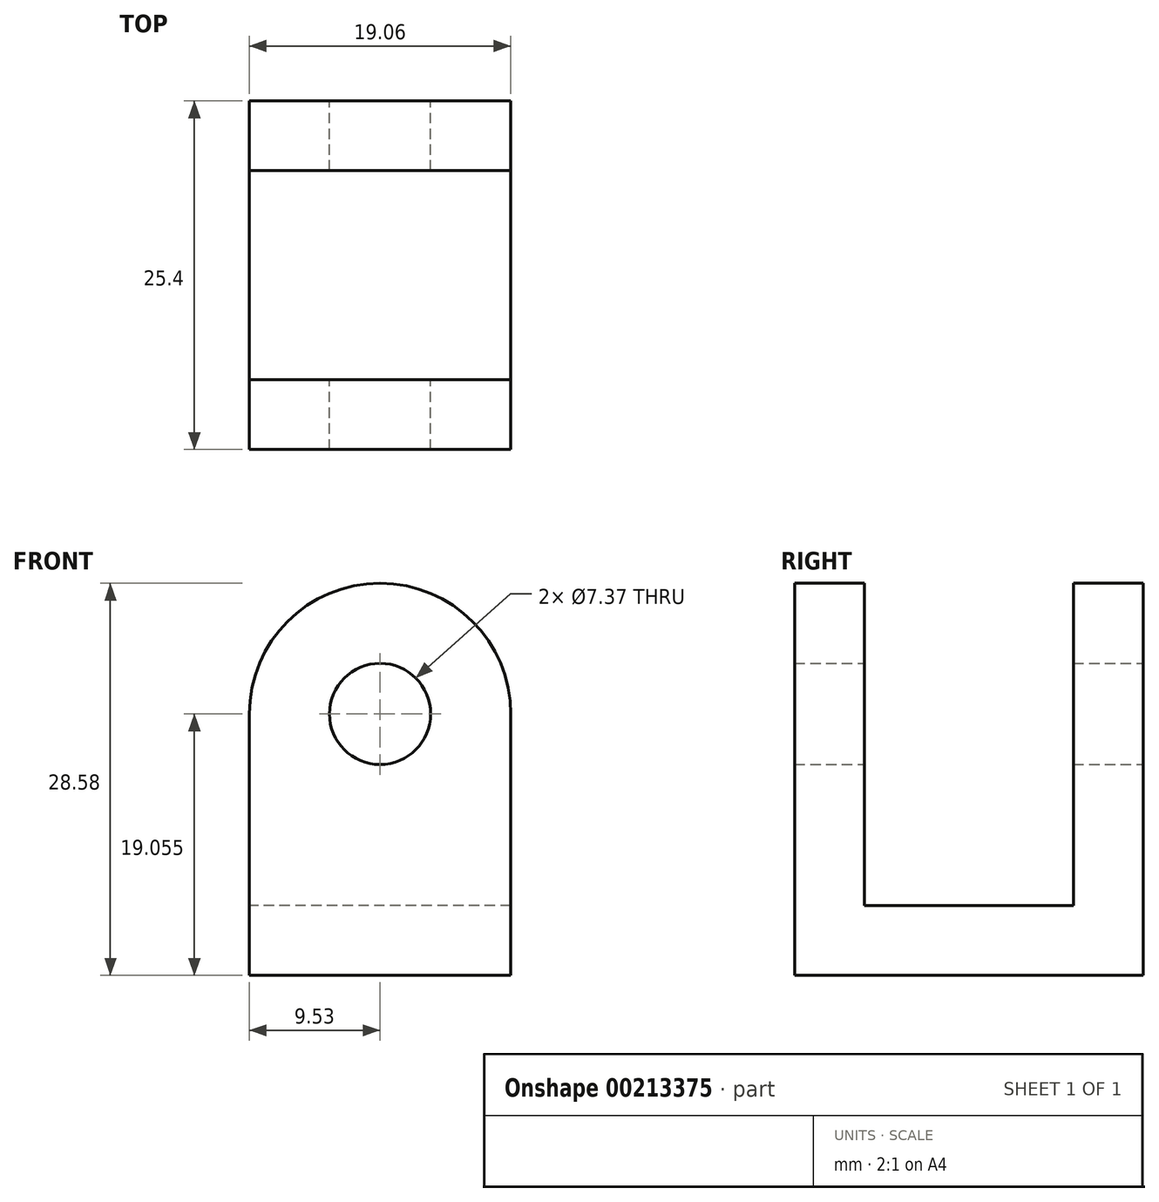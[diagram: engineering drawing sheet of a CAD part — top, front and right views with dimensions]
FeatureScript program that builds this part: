
annotation { "Feature Type Name" : "Feature", "Feature Type Description" : "" }
export const myFeature = defineFeature(function(context is Context, id is Id, definition is map)
    precondition{}
    {
        {
            var Q0;
            Q0=qCreatedBy(makeId("Front.planeOp"),FACE);
            var sketch = newSketch(context, id + "F0", { "sketchPlane" : qUnion([Q0])});
            skLineSegment(sketch, "E0.bottom", {"start": v(9.53, 9.53) * mm, "end": v(-9.52, 9.53) * mm});
            skLineSegment(sketch, "E0.top", {"start": v(9.52, -9.53) * mm, "end": v(-9.53, -9.53) * mm});
            skLineSegment(sketch, "E0.left", {"start": v(9.53, 9.53) * mm, "end": v(9.52, -9.53) * mm});
            skLineSegment(sketch, "E0.right", {"start": v(-9.52, 9.53) * mm, "end": v(-9.53, -9.53) * mm});
            skPoint(sketch, "E0.middle", {"position": v(0, 0) * mm});
            skCircle(sketch, "E1", {"center": v(0, 9.53) * mm, "radius": 9.53 * mm});
            skCircle(sketch, "E2", {"center": v(0, 9.53) * mm, "radius": 3.69 * mm});
            skSolve(sketch);
        }
        {
            var Q0;
            {var subQ0=sQuery(id+"F0.wireOp",EDGE,"E0.bottom");Q0=makeQuery(id+"F0.imprint","IMPRINT",FACE,{"disambiguationData":[TD([[makeQuery(id+"F0.imprint","IMPRINT",EDGE,{"derivedFrom":subQ0}),-1.0]])]});}
            var Q1;
            Q1=makeQuery(id+"F0.imprint","IMPRINT",FACE,{"disambiguationData":[TD([[makeQuery(id+"F0.imprint","IMPRINT",EDGE,{"derivedFrom":sQuery(id+"F0.wireOp",EDGE,"E0.top")}),-1.0]])]});
            var Q2;
            {var subQ0=sQuery(id+"F0.wireOp",EDGE,"E0.bottom");Q2=makeQuery(id+"F0.imprint","IMPRINT",FACE,{"disambiguationData":[TD([[makeQuery(id+"F0.imprint","IMPRINT",EDGE,{"derivedFrom":subQ0}),1.0]])]});}
            extrude(context, id + "F1", {"entities" : qUnion([Q0, Q1, Q2]), "depth" : 25.4 * mm});
        }
        {
            var Q0;
            Q0=qCreatedBy(makeId("Right.planeOp"),FACE);
            var sketch = newSketch(context, id + "F2", { "sketchPlane" : qUnion([Q0])});
            skLineSegment(sketch, "E3.bottom", {"start": v(-20.32, -4.44) * mm, "end": v(-5.08, -4.44) * mm});
            skLineSegment(sketch, "E3.top", {"start": v(-20.32, 23.13) * mm, "end": v(-5.08, 23.13) * mm});
            skLineSegment(sketch, "E3.left", {"start": v(-20.32, -4.44) * mm, "end": v(-20.32, 23.13) * mm});
            skLineSegment(sketch, "E3.right", {"start": v(-5.08, -4.44) * mm, "end": v(-5.08, 23.13) * mm});
            skSolve(sketch);
        }
        {
            var Q0;
            Q0=makeQuery(id+"F2.imprint","IMPRINT",FACE,{"disambiguationData":[TD([[makeQuery(id+"F2.imprint","IMPRINT",EDGE,{"derivedFrom":sQuery(id+"F2.wireOp",EDGE,"E3.bottom")}),1.0]])]});
            extrude(context, id + "F3", {"entities" : qUnion([Q0]), "operationType" : NewBodyOperationType.REMOVE, "endBound" : BoundingType.THROUGH_ALL, "depth" : 25.4 * mm, "hasSecondDirection" : true, "secondDirectionBound" : SecondDirectionBoundingType.THROUGH_ALL, "secondDirectionOppositeDirection" : true, "secondDirectionDepth" : 25.4 * mm});
        }
    });
